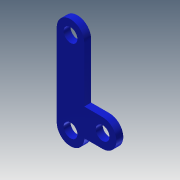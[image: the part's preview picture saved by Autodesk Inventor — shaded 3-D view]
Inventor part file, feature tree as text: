
AUTODESK INVENTOR PART (.ipt)
format: ipt  version: 2015 (Build 190159000, 159)  size: 172,544 bytes
history: native  units: mm
features: extrude x9, sketch x9
ambient origin geometry x8: Origin, YZ Plane, XZ Plane, XY Plane, X Axis, Y Axis, Z Axis, Center Point
bodies: Solid1 (feature_tree)
feature tree (18):
  extrude  "Extrusion1"  Depth=6.0mm
  extrude  "Extrusion2"  Depth=6.0mm
  extrude  "Extrusion3"  Depth=4.0mm
  extrude  "Extrusion4"  Depth=3.0mm
  extrude  "Extrusion5"  Depth=1.5mm TaperAngle=0.0deg
  extrude  "Extrusion6"  Depth=3.0mm
  extrude  "Extrusion7"  Depth=6.0mm
  extrude  "Extrusion8"  Depth=1.5mm
  extrude  "Extrusion9"  Depth=3.0mm
  sketch  "Sketch1"  dims[d0=6.0mm d1=18.0mm]
  sketch  "Sketch2"  dims[d2=6.0mm d4=6.0mm]
  sketch  "Sketch3"  dims[d5=4.0mm d6=4.0mm]
  sketch  "Sketch4"  dims[d7=2.0mm d10=3.0mm]
  sketch  "Sketch5"  dims[d11=6.0mm d12=1.5mm d13=0.0mm]
  sketch  "Sketch6"  dims[d14=3.0mm d15=3.0mm]
  sketch  "Sketch7"  dims[d16=4.0mm d17=6.0mm]
  sketch  "Sketch8"  dims[d18=1.5mm d19=0.0mm d20=4.0mm]
  sketch  "Sketch9"  dims[d21=6.0mm d22=4.0mm d23=1.5mm d24=0.0mm d25=3.0mm d26=1.5mm d27=0.0mm d28=0.2mm d29=0.2mm d30=0.2mm d31=1.5mm d32=0.0mm d33=3.0mm d34=3.0mm d35=3.0mm d36=2.0mm d37=0.0mm d38=4.0mm d39=3.0mm d40=2.0mm d41=0.0mm d42=2.0mm d43=0.0mm d44=0.5mm d45=0.0mm]
